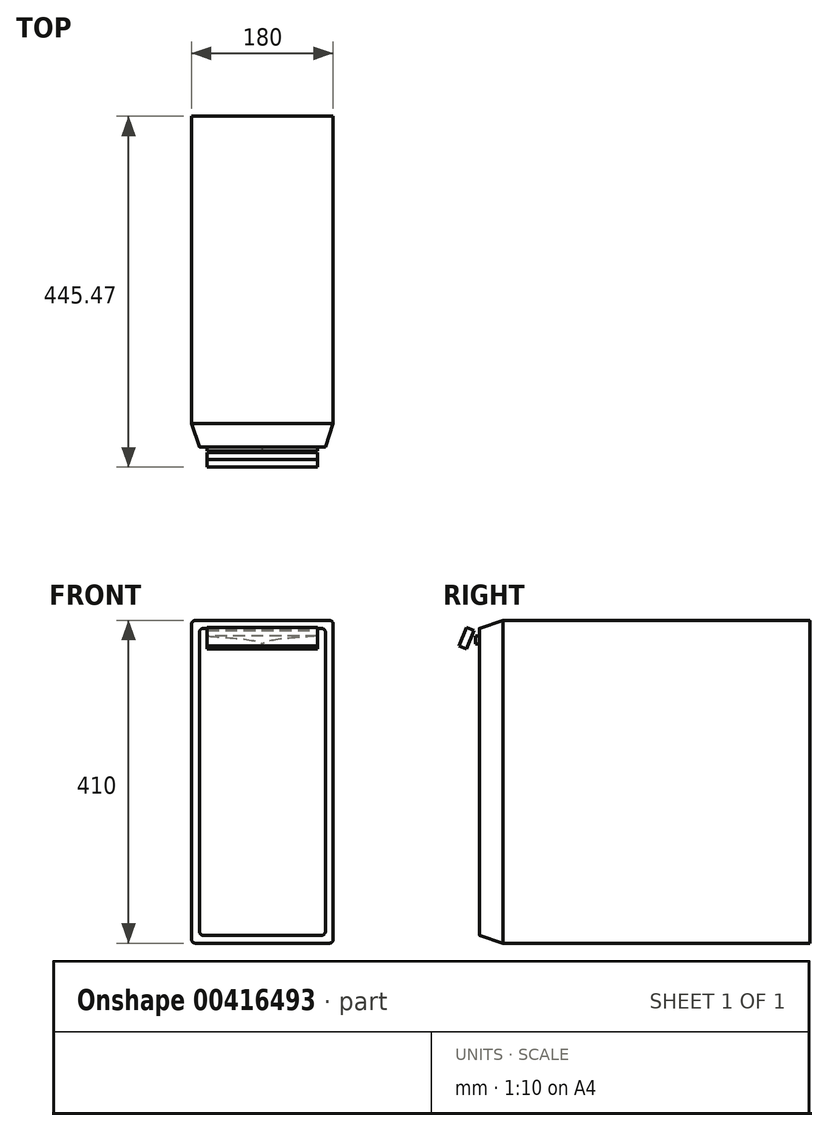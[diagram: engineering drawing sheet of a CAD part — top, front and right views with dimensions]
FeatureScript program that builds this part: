
annotation { "Feature Type Name" : "Feature", "Feature Type Description" : "" }
export const myFeature = defineFeature(function(context is Context, id is Id, definition is map)
    precondition{}
    {
        {
            var Q0;
            Q0=qCreatedBy(makeId("Top.planeOp"),FACE);
            var sketch = newSketch(context, id + "F0", { "sketchPlane" : qUnion([Q0])});
            skLineSegment(sketch, "E0.bottom", {"start": v(-90, 195) * mm, "end": v(90, 195) * mm});
            skLineSegment(sketch, "E0.top", {"start": v(-90, -195) * mm, "end": v(90, -195) * mm});
            skLineSegment(sketch, "E0.left", {"start": v(-90, 195) * mm, "end": v(-90, -195) * mm});
            skLineSegment(sketch, "E0.right", {"start": v(90, 195) * mm, "end": v(90, -195) * mm});
            skSolve(sketch);
        }
        {
            var Q0;
            Q0=makeQuery(id+"F0.imprint","IMPRINT",FACE,{"disambiguationData":[TD([[makeQuery(id+"F0.imprint","IMPRINT",EDGE,{"derivedFrom":sQuery(id+"F0.wireOp",EDGE,"E0.bottom")}),-1.0]])]});
            extrude(context, id + "F1", {"entities" : qUnion([Q0]), "depth" : 410 * mm});
        }
        {
            var Q0;
            Q0=makeQuery(id+"F1.opExtrude","CAP_EDGE",EDGE,{"disambiguationData":[OSD([sQuery(id+"F0.wireOp",EDGE,"E0.right")])],"isStart":false});
            var Q1;
            Q1=makeQuery(id+"F1.opExtrude","CAP_EDGE",EDGE,{"disambiguationData":[OSD([sQuery(id+"F0.wireOp",EDGE,"E0.left")])],"isStart":false});
            var Q2;
            Q2=makeQuery(id+"F1.opExtrude","CAP_EDGE",EDGE,{"disambiguationData":[OSD([sQuery(id+"F0.wireOp",EDGE,"E0.right")])],"isStart":true});
            var Q3;
            Q3=makeQuery(id+"F1.opExtrude","CAP_EDGE",EDGE,{"disambiguationData":[OSD([sQuery(id+"F0.wireOp",EDGE,"E0.left")])],"isStart":true});
            fillet(context, id + "F2", {"entities" : qUnion([Q0, Q1, Q2, Q3]), "radius" : 5 * mm, "tangentPropagation" : true, "allowEdgeOverflow" : false});
        }
        {
            var Q0;
            Q0=qCreatedBy(makeId("Front.planeOp"),FACE);
            cPlane(context, id + "F3", {"entities" : qUnion([Q0]), "cplaneType" : CPlaneType.OFFSET, "offset" : 225 * mm, "width" : 150 * mm, "height" : 150 * mm});
        }
        {
            var Q0;
            Q0=qCreatedBy(id+"F3.planeOp",FACE);
            var sketch = newSketch(context, id + "F4", { "sketchPlane" : qUnion([Q0])});
            skLineSegment(sketch, "E1.bottom", {"start": v(-75, 400) * mm, "end": v(75, 400) * mm});
            skLineSegment(sketch, "E1.top", {"start": v(-75, 10) * mm, "end": v(75, 10) * mm});
            skLineSegment(sketch, "E1.left", {"start": v(-80, 395) * mm, "end": v(-80, 15) * mm});
            skLineSegment(sketch, "E1.right", {"start": v(80, 395) * mm, "end": v(80, 15) * mm});
            skPoint(sketch, "E2.visualSharp", {"position": v(-80, 400) * mm});
            skArc(sketch, "E2.filletArc", {"start": v(-75, 400) * mm, "mid": v(-78.54, 398.54) * mm, "end": v(-80, 395) * mm});
            skPoint(sketch, "E3.visualSharp", {"position": v(80, 400) * mm});
            skArc(sketch, "E3.filletArc", {"start": v(80, 395) * mm, "mid": v(78.54, 398.54) * mm, "end": v(75, 400) * mm});
            skPoint(sketch, "E4.visualSharp", {"position": v(-80, 10) * mm});
            skArc(sketch, "E4.filletArc", {"start": v(-80, 15) * mm, "mid": v(-78.54, 11.46) * mm, "end": v(-75, 10) * mm});
            skPoint(sketch, "E5.visualSharp", {"position": v(80, 10) * mm});
            skArc(sketch, "E5.filletArc", {"start": v(75, 10) * mm, "mid": v(78.54, 11.46) * mm, "end": v(80, 15) * mm});
            skSolve(sketch);
        }
        {
            var Q0;
            Q0=makeQuery(id+"F1.opExtrude","SWEPT_FACE",FACE,{"disambiguationData":[OSD([sQuery(id+"F0.wireOp",EDGE,"E0.top")])]});
            var sketch = newSketch(context, id + "F5", { "sketchPlane" : qUnion([Q0])});
            skLineSegment(sketch, "E6.bottom", {"start": v(-85, 410) * mm, "end": v(85, 410) * mm});
            skLineSegment(sketch, "E6.top", {"start": v(-85, 0) * mm, "end": v(85, 0) * mm});
            skLineSegment(sketch, "E6.left", {"start": v(-90, 405) * mm, "end": v(-90, 5) * mm});
            skLineSegment(sketch, "E6.right", {"start": v(90, 405) * mm, "end": v(90, 5) * mm});
            skPoint(sketch, "E7.visualSharp", {"position": v(-90, 410) * mm});
            skArc(sketch, "E7.filletArc", {"start": v(-85, 410) * mm, "mid": v(-88.54, 408.54) * mm, "end": v(-90, 405) * mm});
            skPoint(sketch, "E8.visualSharp", {"position": v(90, 410) * mm});
            skArc(sketch, "E8.filletArc", {"start": v(90, 405) * mm, "mid": v(88.54, 408.54) * mm, "end": v(85, 410) * mm});
            skPoint(sketch, "E9.visualSharp", {"position": v(90, 0) * mm});
            skArc(sketch, "E9.filletArc", {"start": v(85, 0) * mm, "mid": v(88.54, 1.46) * mm, "end": v(90, 5) * mm});
            skPoint(sketch, "E10.visualSharp", {"position": v(-90, 0) * mm});
            skArc(sketch, "E10.filletArc", {"start": v(-90, 5) * mm, "mid": v(-88.54, 1.46) * mm, "end": v(-85, 0) * mm});
            skSolve(sketch);
        }
        {
            var Q1;
            Q1 = qSketchRegion(id + "F4", true);
            var Q2;
            Q2 = qSketchRegion(id + "F5", true);
            loft(context, id + "F6", {"operationType" : NewBodyOperationType.ADD, "sheetProfilesArray" : [{ "sheetProfileEntities" : qUnion([Q1]) }, { "sheetProfileEntities" : qUnion([Q2]) }]});
        }
        {
            var Q0;
            Q0=makeQuery(id+"F6.opLoft","CAP_FACE",FACE,{"disambiguationData":[OSD([makeQuery(id+"F4.imprint","IMPRINT",FACE,{"disambiguationData":[TD([[makeQuery(id+"F4.imprint","IMPRINT",EDGE,{"derivedFrom":sQuery(id+"F4.wireOp",EDGE,"E1.bottom")}),-1.0]])]})])],"isStart":true});
            var sketch = newSketch(context, id + "F7", { "sketchPlane" : qUnion([Q0])});
            skLineSegment(sketch, "E11.0", {"start": v(70, 390) * mm, "end": v(-70, 390) * mm});
            skLineSegment(sketch, "E11.1", {"start": v(-70, 390) * mm, "end": v(0, 380) * mm});
            skLineSegment(sketch, "E11.2", {"start": v(0, 380) * mm, "end": v(70, 390) * mm});
            skFitSpline(sketch, "E12", {"points": [v(-70, 390) * mm, v(0, 380) * mm, v(0, 374.46) * mm], "startDerivative": vector(124.59, -7.9) * mm, "endDerivative": vector(-9.8, -26.7) * mm});
            skLineSegment(sketch, "E13", {"start": v(0, 380) * mm, "end": v(0, 390) * mm});
            skFitSpline(sketch, "E14.MirrorCS", {"points": [v(70, 390) * mm, v(0, 380) * mm, v(0, 374.46) * mm], "startDerivative": vector(-124.59, -7.9) * mm, "endDerivative": vector(9.8, -26.7) * mm});
            skLineSegment(sketch, "E15.bottom", {"start": v(-70, 347.2) * mm, "end": v(70, 347.2) * mm});
            skLineSegment(sketch, "E15.top", {"start": v(-70, 337.2) * mm, "end": v(70, 337.2) * mm});
            skLineSegment(sketch, "E15.left", {"start": v(-70, 347.2) * mm, "end": v(-70, 337.2) * mm});
            skLineSegment(sketch, "E15.right", {"start": v(70, 347.2) * mm, "end": v(70, 337.2) * mm});
            skSolve(sketch);
        }
        {
            var Q0;
            {var subQ2=sQuery(id+"F7.wireOp",EDGE,"E13");Q0=makeQuery(id+"F7.imprint","IMPRINT",FACE,{"disambiguationData":[TD([[makeQuery(id+"F7.imprint","IMPRINT",EDGE,{"derivedFrom":subQ2}),-1.0]])]});}
            var Q1;
            {var subQ0=sQuery(id+"F7.wireOp",EDGE,"E12");Q1=makeQuery(id+"F7.imprint","IMPRINT",FACE,{"disambiguationData":[TD([[makeQuery(id+"F7.imprint","IMPRINT",EDGE,{"derivedFrom":subQ0}),1.0]])]});}
            extrude(context, id + "F8", {"entities" : qUnion([Q0, Q1]), "depth" : 5 * mm});
        }
        {
            var Q0;
            Q0=makeQuery(id+"F7.imprint","IMPRINT",FACE,{"disambiguationData":[TD([[makeQuery(id+"F7.imprint","IMPRINT",EDGE,{"derivedFrom":sQuery(id+"F7.wireOp",EDGE,"E15.bottom")}),-1.0]])]});
            extrude(context, id + "F9", {"entities" : qUnion([Q0]), "depth" : 25 * mm});
        }
        {
            var Q0;
            Q0=makeQuery(id+"F9.opExtrude","SWEPT_BODY",BODY,{"disambiguationData":[OSD([sQuery(id+"F7.wireOp",EDGE,"E15.bottom"),sQuery(id+"F7.wireOp",EDGE,"E15.top"),sQuery(id+"F7.wireOp",EDGE,"E15.left"),sQuery(id+"F7.wireOp",EDGE,"E15.right")])]});
            var Q1;
            Q1=makeQuery(id+"F9.opExtrude","CAP_EDGE",EDGE,{"disambiguationData":[OSD([sQuery(id+"F7.wireOp",EDGE,"E15.top")])],"isStart":false});
            transform(context, id + "F10", {"entities" : qUnion([Q0]), "transformType" : TransformType.ROTATION, "transformAxis" : qUnion([Q1]), "angle" : 67.9 * degree, "makeCopy" : false});
        }
        {
            var Q0;
            Q0=makeQuery(id+"F9.opExtrude","SWEPT_BODY",BODY,{"disambiguationData":[OSD([sQuery(id+"F7.wireOp",EDGE,"E15.bottom"),sQuery(id+"F7.wireOp",EDGE,"E15.top"),sQuery(id+"F7.wireOp",EDGE,"E15.left"),sQuery(id+"F7.wireOp",EDGE,"E15.right")])]});
            transform(context, id + "F11", {"entities" : qUnion([Q0]), "transformType" : TransformType.TRANSLATION_3D, "dx" : 0 * mm, "dy" : 8.8 * mm, "dz" : 36.7 * mm, "makeCopy" : false});
        }
    });
